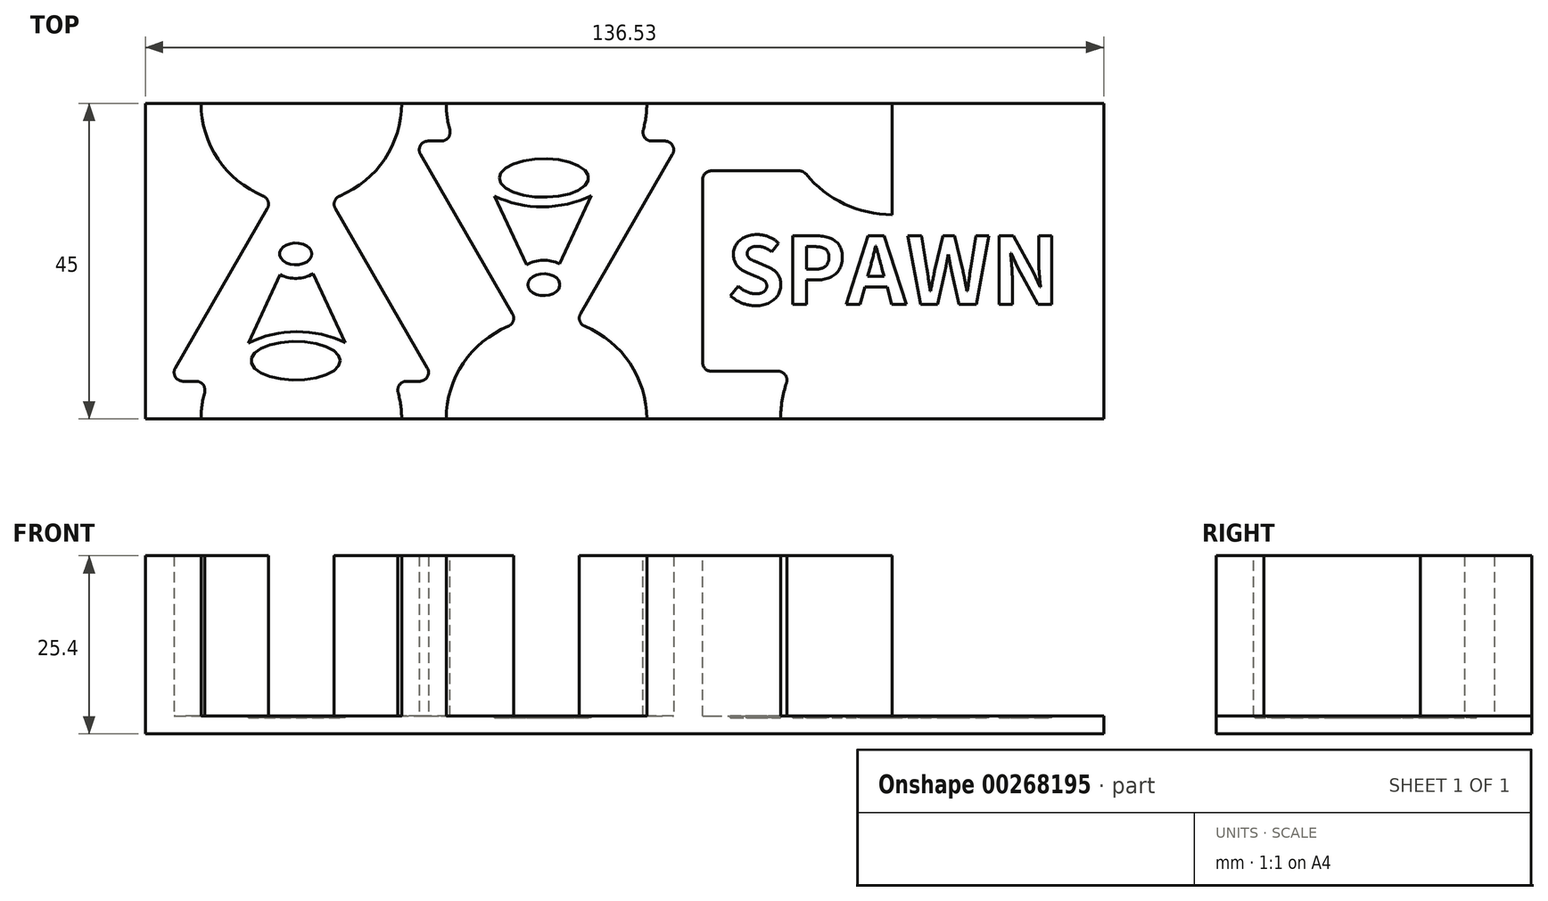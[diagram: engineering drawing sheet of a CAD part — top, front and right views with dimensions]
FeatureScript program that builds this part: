
annotation { "Feature Type Name" : "Feature", "Feature Type Description" : "" }
export const myFeature = defineFeature(function(context is Context, id is Id, definition is map)
    precondition{}
    {
        {
            var Q0;
            Q0=qCreatedBy(makeId("Top.planeOp"),FACE);
            var sketch = newSketch(context, id + "F0", { "sketchPlane" : qUnion([Q0])});
            skLineSegment(sketch, "E0.bottom", {"start": v(0, 0) * mm, "end": v(136.53, 0) * mm});
            skLineSegment(sketch, "E0.top", {"start": v(0, 45) * mm, "end": v(136.53, 45) * mm});
            skLineSegment(sketch, "E0.left", {"start": v(0, 0) * mm, "end": v(0, 45) * mm});
            skLineSegment(sketch, "E0.right", {"start": v(136.53, 0) * mm, "end": v(136.53, 45) * mm});
            skSolve(sketch);
        }
        {
            var Q0;
            Q0=makeQuery(id+"F0.imprint","IMPRINT",FACE,{"disambiguationData":[TD([[makeQuery(id+"F0.imprint","IMPRINT",EDGE,{"derivedFrom":sQuery(id+"F0.wireOp",EDGE,"E0.bottom")}),1.0]])]});
            extrude(context, id + "F1", {"entities" : qUnion([Q0]), "depth" : 25.4 * mm});
        }
        {
            var Q0;
            Q0=makeQuery(id+"F1.opExtrude","CAP_FACE",FACE,{"disambiguationData":[OSD([sQuery(id+"F0.wireOp",EDGE,"E0.bottom"),sQuery(id+"F0.wireOp",EDGE,"E0.top"),sQuery(id+"F0.wireOp",EDGE,"E0.left"),sQuery(id+"F0.wireOp",EDGE,"E0.right")])],"isStart":false});
            var sketch = newSketch(context, id + "F2", { "sketchPlane" : qUnion([Q0])});
            skCircle(sketch, "E1.cCircle", {"center": v(22.23, 16.38) * mm, "radius": 11 * mm, "construction": true});
            skLineSegment(sketch, "E1.0", {"start": v(22.23, 38.38) * mm, "end": v(41.28, 5.38) * mm});
            skLineSegment(sketch, "E1.1", {"start": v(41.28, 5.38) * mm, "end": v(3.17, 5.38) * mm});
            skLineSegment(sketch, "E1.2", {"start": v(3.17, 5.38) * mm, "end": v(22.23, 38.38) * mm});
            skPoint(sketch, "E1.0.midPoint", {"position": v(31.75, 21.88) * mm});
            skLineSegment(sketch, "E2", {"start": v(0, 22.5) * mm, "end": v(136.53, 22.5) * mm, "construction": true});
            skPoint(sketch, "E2.startSnap0", {"position": v(0, 22.5) * mm});
            skLineSegment(sketch, "E3", {"start": v(22.23, 45) * mm, "end": v(22.22, 0) * mm, "construction": true});
            skPoint(sketch, "E3.endSnap0", {"position": v(22.23, 5.38) * mm});
            skCircle(sketch, "E4", {"center": v(22.23, 45) * mm, "radius": 14.29 * mm});
            skCircle(sketch, "E5", {"center": v(22.22, 0) * mm, "radius": 14.29 * mm});
            skCircle(sketch, "E6.cCircle", {"center": v(57.15, 28.62) * mm, "radius": 11 * mm, "construction": true});
            skLineSegment(sketch, "E6.0", {"start": v(57.15, 6.63) * mm, "end": v(38.1, 39.62) * mm});
            skLineSegment(sketch, "E6.1", {"start": v(38.1, 39.62) * mm, "end": v(76.2, 39.62) * mm});
            skLineSegment(sketch, "E6.2", {"start": v(76.2, 39.62) * mm, "end": v(57.15, 6.63) * mm});
            skPoint(sketch, "E6.0.midPoint", {"position": v(47.63, 23.12) * mm});
            skLineSegment(sketch, "E7", {"start": v(136.53, 22.5) * mm, "end": v(0, 22.5) * mm, "construction": true});
            skPoint(sketch, "E7.startSnap0", {"position": v(122.49, -12.24) * mm});
            skLineSegment(sketch, "E8", {"start": v(57.15, 0) * mm, "end": v(57.15, 45) * mm, "construction": true});
            skPoint(sketch, "E8.endSnap0", {"position": v(57.15, 39.62) * mm});
            skCircle(sketch, "E9", {"center": v(57.15, 0) * mm, "radius": 14.29 * mm});
            skCircle(sketch, "E10", {"center": v(57.15, 45) * mm, "radius": 14.29 * mm});
            skLineSegment(sketch, "E11.bottom", {"start": v(79.38, 35.38) * mm, "end": v(133.35, 35.38) * mm});
            skLineSegment(sketch, "E11.top", {"start": v(79.38, 6.8) * mm, "end": v(133.35, 6.8) * mm});
            skLineSegment(sketch, "E11.left", {"start": v(79.38, 35.38) * mm, "end": v(79.38, 6.8) * mm});
            skLineSegment(sketch, "E11.right", {"start": v(133.35, 35.38) * mm, "end": v(133.35, 6.8) * mm});
            skCircle(sketch, "E12", {"center": v(106.36, 45) * mm, "radius": 15.88 * mm});
            skPoint(sketch, "E13.startSnap0", {"position": v(106.36, 6.8) * mm});
            skLineSegment(sketch, "E14", {"start": v(106.36, 0) * mm, "end": v(106.36, 45) * mm});
            skCircle(sketch, "E15", {"center": v(106.36, 0) * mm, "radius": 15.88 * mm});
            skSolve(sketch);
        }
        {
            var Q0;
            {var subQ1=sQuery(id+"F2.wireOp",EDGE,"E1.1");var subQ7=sQuery(id+"F2.wireOp",EDGE,"E1.0");var subQ8=makeQuery(id+"F2.imprint","INTERSECT",VERTEX,{"derivedFrom":[subQ7,subQ1]});Q0=makeQuery(id+"F2.imprint","IMPRINT",FACE,{"disambiguationData":[TD([[makeQuery(id+"F2.imprint","IMPRINT",EDGE,{"disambiguationData":[TD([[subQ8,1.0]])],"derivedFrom":subQ7}),-1.0]])]});}
            var Q1;
            {var subQ0=sQuery(id+"F2.wireOp",EDGE,"E5");var subQ1=sQuery(id+"F2.wireOp",EDGE,"E1.1");var subQ2=makeQuery(id+"F2.imprint","INTERSECT",VERTEX,{"disambiguationData":[OD(0.0)],"derivedFrom":[subQ1,subQ0]});Q1=makeQuery(id+"F2.imprint","IMPRINT",FACE,{"disambiguationData":[TD([[makeQuery(id+"F2.imprint","IMPRINT",EDGE,{"disambiguationData":[TD([[subQ2,-1.0]])],"derivedFrom":subQ1}),-1.0]])]});}
            var Q2;
            {var subQ0=sQuery(id+"F2.wireOp",EDGE,"E5");var subQ1=sQuery(id+"F2.wireOp",EDGE,"E1.1");var subQ2=makeQuery(id+"F2.imprint","INTERSECT",VERTEX,{"disambiguationData":[OD(0.0)],"derivedFrom":[subQ1,subQ0]});Q2=makeQuery(id+"F2.imprint","IMPRINT",FACE,{"disambiguationData":[TD([[makeQuery(id+"F2.imprint","IMPRINT",EDGE,{"disambiguationData":[TD([[subQ2,-1.0]])],"derivedFrom":subQ1}),1.0]])]});}
            var Q3;
            {var subQ1=sQuery(id+"F2.wireOp",EDGE,"E1.0");var subQ5=sQuery(id+"F2.wireOp",EDGE,"E1.2");var subQ8=makeQuery(id+"F2.imprint","INTERSECT",VERTEX,{"derivedFrom":[subQ1,subQ5]});Q3=makeQuery(id+"F2.imprint","IMPRINT",FACE,{"disambiguationData":[TD([[makeQuery(id+"F2.imprint","IMPRINT",EDGE,{"disambiguationData":[TD([[subQ8,-1.0]])],"derivedFrom":subQ1}),1.0]])]});}
            var Q4;
            {var subQ0=sQuery(id+"F2.wireOp",EDGE,"E1.2");var subQ1=sQuery(id+"F2.wireOp",EDGE,"E1.0");var subQ2=makeQuery(id+"F2.imprint","INTERSECT",VERTEX,{"derivedFrom":[subQ1,subQ0]});Q4=makeQuery(id+"F2.imprint","IMPRINT",FACE,{"disambiguationData":[TD([[makeQuery(id+"F2.imprint","IMPRINT",EDGE,{"disambiguationData":[TD([[subQ2,-1.0]])],"derivedFrom":subQ1}),-1.0]])]});}
            var Q5;
            {var subQ0=sQuery(id+"F2.wireOp",EDGE,"E10");var subQ1=sQuery(id+"F2.wireOp",EDGE,"E6.1");var subQ2=makeQuery(id+"F2.imprint","INTERSECT",VERTEX,{"disambiguationData":[OD(0.0)],"derivedFrom":[subQ1,subQ0]});Q5=makeQuery(id+"F2.imprint","IMPRINT",FACE,{"disambiguationData":[TD([[makeQuery(id+"F2.imprint","IMPRINT",EDGE,{"disambiguationData":[TD([[subQ2,-1.0]])],"derivedFrom":subQ1}),-1.0]])]});}
            var Q6;
            {var subQ0=sQuery(id+"F2.wireOp",EDGE,"E10");var subQ1=sQuery(id+"F2.wireOp",EDGE,"E6.1");var subQ2=makeQuery(id+"F2.imprint","INTERSECT",VERTEX,{"disambiguationData":[OD(0.0)],"derivedFrom":[subQ1,subQ0]});Q6=makeQuery(id+"F2.imprint","IMPRINT",FACE,{"disambiguationData":[TD([[makeQuery(id+"F2.imprint","IMPRINT",EDGE,{"disambiguationData":[TD([[subQ2,-1.0]])],"derivedFrom":subQ1}),1.0]])]});}
            var Q7;
            {var subQ1=sQuery(id+"F2.wireOp",EDGE,"E6.1");var subQ5=sQuery(id+"F2.wireOp",EDGE,"E6.0");var subQ6=makeQuery(id+"F2.imprint","INTERSECT",VERTEX,{"derivedFrom":[subQ5,subQ1]});Q7=makeQuery(id+"F2.imprint","IMPRINT",FACE,{"disambiguationData":[TD([[makeQuery(id+"F2.imprint","IMPRINT",EDGE,{"disambiguationData":[TD([[subQ6,1.0]])],"derivedFrom":subQ5}),-1.0]])]});}
            var Q8;
            {var subQ0=sQuery(id+"F2.wireOp",EDGE,"E6.2");var subQ1=sQuery(id+"F2.wireOp",EDGE,"E6.0");var subQ2=makeQuery(id+"F2.imprint","INTERSECT",VERTEX,{"derivedFrom":[subQ1,subQ0]});Q8=makeQuery(id+"F2.imprint","IMPRINT",FACE,{"disambiguationData":[TD([[makeQuery(id+"F2.imprint","IMPRINT",EDGE,{"disambiguationData":[TD([[subQ2,-1.0]])],"derivedFrom":subQ1}),-1.0]])]});}
            var Q9;
            {var subQ1=sQuery(id+"F2.wireOp",EDGE,"E6.2");var subQ6=sQuery(id+"F2.wireOp",EDGE,"E6.0");var subQ8=makeQuery(id+"F2.imprint","INTERSECT",VERTEX,{"derivedFrom":[subQ6,subQ1]});Q9=makeQuery(id+"F2.imprint","IMPRINT",FACE,{"disambiguationData":[TD([[makeQuery(id+"F2.imprint","IMPRINT",EDGE,{"disambiguationData":[TD([[subQ8,-1.0]])],"derivedFrom":subQ6}),1.0]])]});}
            var Q10;
            {var subQ5=sQuery(id+"F2.wireOp",EDGE,"E11.left");Q10=makeQuery(id+"F2.imprint","IMPRINT",FACE,{"disambiguationData":[TD([[makeQuery(id+"F2.imprint","IMPRINT",EDGE,{"derivedFrom":subQ5}),1.0]])]});}
            var Q11;
            {var subQ0=sQuery(id+"F2.wireOp",EDGE,"E12");var subQ1=sQuery(id+"F2.wireOp",EDGE,"E11.bottom");var subQ2=makeQuery(id+"F2.imprint","INTERSECT",VERTEX,{"disambiguationData":[OD(0.0)],"derivedFrom":[subQ1,subQ0]});Q11=makeQuery(id+"F2.imprint","IMPRINT",FACE,{"disambiguationData":[TD([[makeQuery(id+"F2.imprint","IMPRINT",EDGE,{"disambiguationData":[TD([[subQ2,-1.0]])],"derivedFrom":subQ1}),-1.0]])]});}
            var Q12;
            {var subQ0=sQuery(id+"F2.wireOp",EDGE,"E14");var subQ1=sQuery(id+"F2.wireOp",EDGE,"E11.bottom");var subQ2=makeQuery(id+"F2.imprint","INTERSECT",VERTEX,{"derivedFrom":[subQ1,subQ0]});Q12=makeQuery(id+"F2.imprint","IMPRINT",FACE,{"disambiguationData":[TD([[makeQuery(id+"F2.imprint","IMPRINT",EDGE,{"disambiguationData":[TD([[subQ2,-1.0]])],"derivedFrom":subQ1}),-1.0]])]});}
            var Q13;
            {var subQ0=sQuery(id+"F2.wireOp",EDGE,"E14");var subQ1=sQuery(id+"F2.wireOp",EDGE,"E11.bottom");var subQ2=makeQuery(id+"F2.imprint","INTERSECT",VERTEX,{"derivedFrom":[subQ1,subQ0]});Q13=makeQuery(id+"F2.imprint","IMPRINT",FACE,{"disambiguationData":[TD([[makeQuery(id+"F2.imprint","IMPRINT",EDGE,{"disambiguationData":[TD([[subQ2,-1.0]])],"derivedFrom":subQ1}),1.0]])]});}
            var Q14;
            {var subQ0=sQuery(id+"F2.wireOp",EDGE,"E12");var subQ1=sQuery(id+"F2.wireOp",EDGE,"E11.bottom");var subQ2=makeQuery(id+"F2.imprint","INTERSECT",VERTEX,{"disambiguationData":[OD(0.0)],"derivedFrom":[subQ1,subQ0]});Q14=makeQuery(id+"F2.imprint","IMPRINT",FACE,{"disambiguationData":[TD([[makeQuery(id+"F2.imprint","IMPRINT",EDGE,{"disambiguationData":[TD([[subQ2,-1.0]])],"derivedFrom":subQ1}),1.0]])]});}
            var Q15;
            {var subQ0=sQuery(id+"F2.wireOp",EDGE,"E11.right");Q15=makeQuery(id+"F2.imprint","IMPRINT",FACE,{"disambiguationData":[TD([[makeQuery(id+"F2.imprint","IMPRINT",EDGE,{"derivedFrom":subQ0}),-1.0]])]});}
            var Q16;
            {var subQ0=sQuery(id+"F2.wireOp",EDGE,"E14");var subQ1=sQuery(id+"F2.wireOp",EDGE,"E11.top");var subQ2=makeQuery(id+"F2.imprint","INTERSECT",VERTEX,{"derivedFrom":[subQ1,subQ0]});Q16=makeQuery(id+"F2.imprint","IMPRINT",FACE,{"disambiguationData":[TD([[makeQuery(id+"F2.imprint","IMPRINT",EDGE,{"disambiguationData":[TD([[subQ2,-1.0]])],"derivedFrom":subQ1}),1.0]])]});}
            var Q17;
            {var subQ0=sQuery(id+"F2.wireOp",EDGE,"E15");var subQ1=sQuery(id+"F2.wireOp",EDGE,"E11.top");var subQ2=makeQuery(id+"F2.imprint","INTERSECT",VERTEX,{"disambiguationData":[OD(0.0)],"derivedFrom":[subQ1,subQ0]});Q17=makeQuery(id+"F2.imprint","IMPRINT",FACE,{"disambiguationData":[TD([[makeQuery(id+"F2.imprint","IMPRINT",EDGE,{"disambiguationData":[TD([[subQ2,-1.0]])],"derivedFrom":subQ1}),1.0]])]});}
            var Q18;
            {var subQ0=sQuery(id+"F2.wireOp",EDGE,"E15");var subQ1=sQuery(id+"F2.wireOp",EDGE,"E11.top");var subQ2=makeQuery(id+"F2.imprint","INTERSECT",VERTEX,{"disambiguationData":[OD(0.0)],"derivedFrom":[subQ1,subQ0]});Q18=makeQuery(id+"F2.imprint","IMPRINT",FACE,{"disambiguationData":[TD([[makeQuery(id+"F2.imprint","IMPRINT",EDGE,{"disambiguationData":[TD([[subQ2,-1.0]])],"derivedFrom":subQ1}),-1.0]])]});}
            var Q19;
            {var subQ0=sQuery(id+"F2.wireOp",EDGE,"E14");var subQ1=sQuery(id+"F2.wireOp",EDGE,"E11.top");var subQ2=makeQuery(id+"F2.imprint","INTERSECT",VERTEX,{"derivedFrom":[subQ1,subQ0]});Q19=makeQuery(id+"F2.imprint","IMPRINT",FACE,{"disambiguationData":[TD([[makeQuery(id+"F2.imprint","IMPRINT",EDGE,{"disambiguationData":[TD([[subQ2,-1.0]])],"derivedFrom":subQ1}),-1.0]])]});}
            extrude(context, id + "F3", {"entities" : qUnion([Q0, Q1, Q2, Q3, Q4, Q5, Q6, Q7, Q8, Q9, Q10, Q11, Q12, Q13, Q14, Q15, Q16, Q17, Q18, Q19]), "operationType" : NewBodyOperationType.REMOVE, "oppositeDirection" : true, "depth" : 22.86 * mm});
        }
        {
            var Q0;
            Q0=makeQuery(id+"F3.boolean.opBoolean","COPY",FACE,{"derivedFrom":makeQuery(id+"F3.opExtrude","CAP_FACE",FACE,{"disambiguationData":[OSD([sQuery(id+"F0.wireOp",EDGE,"E0.bottom"),sQuery(id+"F0.wireOp",EDGE,"E0.top"),sQuery(id+"F2.wireOp",EDGE,"E11.bottom"),sQuery(id+"F2.wireOp",EDGE,"E11.top"),sQuery(id+"F2.wireOp",EDGE,"E11.left"),sQuery(id+"F2.wireOp",EDGE,"E11.right"),sQuery(id+"F2.wireOp",EDGE,"E12"),sQuery(id+"F2.wireOp",EDGE,"E15")])],"isStart":false})});
            var sketch = newSketch(context, id + "F4", { "sketchPlane" : qUnion([Q0])});
            skText(sketch, "E16", { "text": "SPAWN", "fontName": "NotoSansCJKsc-Bold.otf"});
            skLineSegment(sketch, "E17", {"start": v(106.36, 50.68) * mm, "end": v(106.36, -4.65) * mm, "construction": true});
            skPoint(sketch, "E17.startSnap0", {"position": v(106.36, 45) * mm});
            skPoint(sketch, "E17.endSnap0", {"position": v(106.36, 0) * mm});
            skLineSegment(sketch, "E18", {"start": v(79.38, 21.1) * mm, "end": v(133.35, 21.1) * mm, "construction": true});
            skPoint(sketch, "E18.startSnap0", {"position": v(82.8, 21.1) * mm});
            skPoint(sketch, "E18.endSnap0", {"position": v(129.92, 21.1) * mm});
            skLineSegment(sketch, "E19", {"start": v(14.67, 10.85) * mm, "end": v(19.2, 20.57) * mm});
            skLineSegment(sketch, "E20", {"start": v(23.9, 20.71) * mm, "end": v(28.48, 10.9) * mm});
            skArc(sketch, "E21", {"start": v(28.48, 10.9) * mm, "mid": v(21.57, 12.43) * mm, "end": v(14.67, 10.85) * mm});
            skEllipse(sketch, "E22", {"center": v(21.42, 23.54) * mm, "majorRadius": 2.29 * mm, "minorRadius": 1.56 * mm, "majorAxis": v(1, 0)});
            skArc(sketch, "E23", {"start": v(19.2, 20.57) * mm, "mid": v(21.57, 20.04) * mm, "end": v(23.9, 20.71) * mm});
            skEllipse(sketch, "E24", {"center": v(21.42, 8.32) * mm, "majorRadius": 6.36 * mm, "minorRadius": 2.75 * mm, "majorAxis": v(1, 0)});
            skLineSegment(sketch, "E25", {"start": v(63.52, 31.83) * mm, "end": v(59, 22.11) * mm});
            skLineSegment(sketch, "E26", {"start": v(54.3, 21.96) * mm, "end": v(49.71, 31.78) * mm});
            skArc(sketch, "E27", {"start": v(49.71, 31.78) * mm, "mid": v(56.62, 30.24) * mm, "end": v(63.52, 31.83) * mm});
            skEllipse(sketch, "E28", {"center": v(56.78, 19.14) * mm, "majorRadius": 2.29 * mm, "minorRadius": 1.56 * mm, "majorAxis": v(-1, 0)});
            skArc(sketch, "E29", {"start": v(59, 22.11) * mm, "mid": v(56.62, 22.63) * mm, "end": v(54.3, 21.96) * mm});
            skEllipse(sketch, "E30", {"center": v(56.78, 34.36) * mm, "majorRadius": 6.36 * mm, "minorRadius": 2.75 * mm, "majorAxis": v(-1, 0)});
            const initialGuessF4  = {"E16": [0.0828, 0.01633, 1, 0, 0.00952]};
            skSetInitialGuess(sketch, initialGuessF4);
            skSolve(sketch);
        }
        {
            var Q0;
            Q0=makeQuery(id+"F4.imprint","IMPRINT",FACE,{"disambiguationData":[TD([[makeQuery(id+"F4.imprint","IMPRINT",EDGE,{"derivedFrom":sQuery(id+"F4.wireOp",EDGE,"E16.sketch_text.stroke-0")}),1.0]])]});
            var Q1;
            Q1=makeQuery(id+"F4.imprint","IMPRINT",FACE,{"disambiguationData":[TD([[makeQuery(id+"F4.imprint","IMPRINT",EDGE,{"derivedFrom":sQuery(id+"F4.wireOp",EDGE,"E16.sketch_text.stroke-16")}),1.0]])]});
            var Q2;
            Q2=makeQuery(id+"F4.imprint","IMPRINT",FACE,{"disambiguationData":[TD([[makeQuery(id+"F4.imprint","IMPRINT",EDGE,{"derivedFrom":sQuery(id+"F4.wireOp",EDGE,"E16.sketch_text.stroke-28")}),1.0]])]});
            var Q3;
            Q3=makeQuery(id+"F4.imprint","IMPRINT",FACE,{"disambiguationData":[TD([[makeQuery(id+"F4.imprint","IMPRINT",EDGE,{"derivedFrom":sQuery(id+"F4.wireOp",EDGE,"E16.sketch_text.stroke-42")}),1.0]])]});
            var Q4;
            Q4=makeQuery(id+"F4.imprint","IMPRINT",FACE,{"disambiguationData":[TD([[makeQuery(id+"F4.imprint","IMPRINT",EDGE,{"derivedFrom":sQuery(id+"F4.wireOp",EDGE,"E16.sketch_text.stroke-64")}),1.0]])]});
            var Q5;
            Q5=makeQuery(id+"F4.imprint","IMPRINT",FACE,{"disambiguationData":[TD([[makeQuery(id+"F4.imprint","IMPRINT",EDGE,{"derivedFrom":sQuery(id+"F4.wireOp",EDGE,"E30")}),1.0]])]});
            var Q6;
            Q6=makeQuery(id+"F4.imprint","IMPRINT",FACE,{"disambiguationData":[TD([[makeQuery(id+"F4.imprint","IMPRINT",EDGE,{"derivedFrom":sQuery(id+"F4.wireOp",EDGE,"E25")}),-1.0]])]});
            var Q7;
            Q7=makeQuery(id+"F4.imprint","IMPRINT",FACE,{"disambiguationData":[TD([[makeQuery(id+"F4.imprint","IMPRINT",EDGE,{"derivedFrom":sQuery(id+"F4.wireOp",EDGE,"E28")}),1.0]])]});
            var Q8;
            Q8=makeQuery(id+"F4.imprint","IMPRINT",FACE,{"disambiguationData":[TD([[makeQuery(id+"F4.imprint","IMPRINT",EDGE,{"derivedFrom":sQuery(id+"F4.wireOp",EDGE,"E24")}),1.0]])]});
            var Q9;
            Q9=makeQuery(id+"F4.imprint","IMPRINT",FACE,{"disambiguationData":[TD([[makeQuery(id+"F4.imprint","IMPRINT",EDGE,{"derivedFrom":sQuery(id+"F4.wireOp",EDGE,"E19")}),-1.0]])]});
            var Q10;
            Q10=makeQuery(id+"F4.imprint","IMPRINT",FACE,{"disambiguationData":[TD([[makeQuery(id+"F4.imprint","IMPRINT",EDGE,{"derivedFrom":sQuery(id+"F4.wireOp",EDGE,"E22")}),1.0]])]});
            extrude(context, id + "F5", {"entities" : qUnion([Q0, Q1, Q2, Q3, Q4, Q5, Q6, Q7, Q8, Q9, Q10]), "operationType" : NewBodyOperationType.REMOVE, "oppositeDirection" : true, "depth" : 0.25 * mm});
        }
        {
            var Q0;
            {var subQ0=sQuery(id+"F2.wireOp",EDGE,"E5");var subQ1=sQuery(id+"F2.wireOp",EDGE,"E1.1");Q0=makeQuery(id+"F3.boolean.opBoolean","COPY",EDGE,{"derivedFrom":makeQuery(id+"F3.opExtrude","SWEPT_EDGE",EDGE,{"disambiguationData":[OSD([subQ1,subQ0]),TDD([makeQuery(id+"F2.imprint","INTERSECT",VERTEX,{"disambiguationData":[OD(1.0)],"derivedFrom":[subQ1,subQ0]})])]})});}
            var Q1;
            {var subQ0=sQuery(id+"F2.wireOp",EDGE,"E5");var subQ1=sQuery(id+"F2.wireOp",EDGE,"E1.1");Q1=makeQuery(id+"F3.boolean.opBoolean","COPY",EDGE,{"derivedFrom":makeQuery(id+"F3.opExtrude","SWEPT_EDGE",EDGE,{"disambiguationData":[OSD([subQ1,subQ0]),TDD([makeQuery(id+"F2.imprint","INTERSECT",VERTEX,{"disambiguationData":[OD(0.0)],"derivedFrom":[subQ1,subQ0]})])]})});}
            var Q2;
            Q2=makeQuery(id+"F3.boolean.opBoolean","COPY",EDGE,{"derivedFrom":makeQuery(id+"F3.opExtrude","SWEPT_EDGE",EDGE,{"disambiguationData":[OSD([sQuery(id+"F2.wireOp",EDGE,"E1.2"),sQuery(id+"F2.wireOp",EDGE,"E4")])]})});
            var Q3;
            Q3=makeQuery(id+"F3.boolean.opBoolean","COPY",EDGE,{"derivedFrom":makeQuery(id+"F3.opExtrude","SWEPT_EDGE",EDGE,{"disambiguationData":[OSD([sQuery(id+"F2.wireOp",EDGE,"E1.0"),sQuery(id+"F2.wireOp",EDGE,"E4")])]})});
            var Q4;
            {var subQ0=sQuery(id+"F2.wireOp",EDGE,"E4");var subQ1=sQuery(id+"F0.wireOp",EDGE,"E0.top");Q4=makeQuery(id+"F3.boolean.opBoolean","COPY",EDGE,{"derivedFrom":makeQuery(id+"F3.opExtrude","SWEPT_EDGE",EDGE,{"disambiguationData":[OSD([subQ1,subQ0]),TDD([makeQuery(id+"F2.imprint","INTERSECT",VERTEX,{"disambiguationData":[OD(0.0)],"derivedFrom":[makeQuery(id+"F1.opExtrude","CAP_EDGE",EDGE,{"disambiguationData":[OSD([subQ1])],"isStart":false}),subQ0]})])]})});}
            var Q5;
            {var subQ0=sQuery(id+"F2.wireOp",EDGE,"E4");var subQ1=sQuery(id+"F0.wireOp",EDGE,"E0.top");Q5=makeQuery(id+"F3.boolean.opBoolean","COPY",EDGE,{"derivedFrom":makeQuery(id+"F3.opExtrude","SWEPT_EDGE",EDGE,{"disambiguationData":[OSD([subQ1,subQ0]),TDD([makeQuery(id+"F2.imprint","INTERSECT",VERTEX,{"disambiguationData":[OD(1.0)],"derivedFrom":[makeQuery(id+"F1.opExtrude","CAP_EDGE",EDGE,{"disambiguationData":[OSD([subQ1])],"isStart":false}),subQ0]})])]})});}
            var Q6;
            {var subQ0=sQuery(id+"F2.wireOp",EDGE,"E10");var subQ1=sQuery(id+"F0.wireOp",EDGE,"E0.top");Q6=makeQuery(id+"F3.boolean.opBoolean","COPY",EDGE,{"derivedFrom":makeQuery(id+"F3.opExtrude","SWEPT_EDGE",EDGE,{"disambiguationData":[OSD([subQ1,subQ0]),TDD([makeQuery(id+"F2.imprint","INTERSECT",VERTEX,{"disambiguationData":[OD(0.0)],"derivedFrom":[makeQuery(id+"F1.opExtrude","CAP_EDGE",EDGE,{"disambiguationData":[OSD([subQ1])],"isStart":false}),subQ0]})])]})});}
            var Q7;
            {var subQ0=sQuery(id+"F2.wireOp",EDGE,"E10");var subQ1=sQuery(id+"F2.wireOp",EDGE,"E6.1");Q7=makeQuery(id+"F3.boolean.opBoolean","COPY",EDGE,{"derivedFrom":makeQuery(id+"F3.opExtrude","SWEPT_EDGE",EDGE,{"disambiguationData":[OSD([subQ1,subQ0]),TDD([makeQuery(id+"F2.imprint","INTERSECT",VERTEX,{"disambiguationData":[OD(0.0)],"derivedFrom":[subQ1,subQ0]})])]})});}
            var Q8;
            Q8=makeQuery(id+"F3.boolean.opBoolean","COPY",EDGE,{"derivedFrom":makeQuery(id+"F3.opExtrude","SWEPT_EDGE",EDGE,{"disambiguationData":[OSD([sQuery(id+"F2.wireOp",EDGE,"E6.0"),sQuery(id+"F2.wireOp",EDGE,"E6.1")])]})});
            var Q9;
            Q9=makeQuery(id+"F3.boolean.opBoolean","COPY",EDGE,{"derivedFrom":makeQuery(id+"F3.opExtrude","SWEPT_EDGE",EDGE,{"disambiguationData":[OSD([sQuery(id+"F2.wireOp",EDGE,"E6.0"),sQuery(id+"F2.wireOp",EDGE,"E9")])]})});
            var Q10;
            Q10=makeQuery(id+"F3.boolean.opBoolean","COPY",EDGE,{"derivedFrom":makeQuery(id+"F3.opExtrude","SWEPT_EDGE",EDGE,{"disambiguationData":[OSD([sQuery(id+"F2.wireOp",EDGE,"E1.0"),sQuery(id+"F2.wireOp",EDGE,"E1.1")])]})});
            var Q11;
            Q11=makeQuery(id+"F3.boolean.opBoolean","COPY",EDGE,{"derivedFrom":makeQuery(id+"F3.opExtrude","SWEPT_EDGE",EDGE,{"disambiguationData":[OSD([sQuery(id+"F2.wireOp",EDGE,"E6.1"),sQuery(id+"F2.wireOp",EDGE,"E6.2")])]})});
            var Q12;
            {var subQ0=sQuery(id+"F2.wireOp",EDGE,"E10");var subQ1=sQuery(id+"F2.wireOp",EDGE,"E6.1");Q12=makeQuery(id+"F3.boolean.opBoolean","COPY",EDGE,{"derivedFrom":makeQuery(id+"F3.opExtrude","SWEPT_EDGE",EDGE,{"disambiguationData":[OSD([subQ1,subQ0]),TDD([makeQuery(id+"F2.imprint","INTERSECT",VERTEX,{"disambiguationData":[OD(1.0)],"derivedFrom":[subQ1,subQ0]})])]})});}
            var Q13;
            {var subQ0=sQuery(id+"F2.wireOp",EDGE,"E10");var subQ1=sQuery(id+"F0.wireOp",EDGE,"E0.top");Q13=makeQuery(id+"F3.boolean.opBoolean","COPY",EDGE,{"derivedFrom":makeQuery(id+"F3.opExtrude","SWEPT_EDGE",EDGE,{"disambiguationData":[OSD([subQ1,subQ0]),TDD([makeQuery(id+"F2.imprint","INTERSECT",VERTEX,{"disambiguationData":[OD(1.0)],"derivedFrom":[makeQuery(id+"F1.opExtrude","CAP_EDGE",EDGE,{"disambiguationData":[OSD([subQ1])],"isStart":false}),subQ0]})])]})});}
            var Q14;
            Q14=makeQuery(id+"F3.boolean.opBoolean","COPY",EDGE,{"derivedFrom":makeQuery(id+"F3.opExtrude","SWEPT_EDGE",EDGE,{"disambiguationData":[OSD([sQuery(id+"F2.wireOp",EDGE,"E6.2"),sQuery(id+"F2.wireOp",EDGE,"E9")])]})});
            var Q15;
            {var subQ0=sQuery(id+"F2.wireOp",EDGE,"E9");var subQ1=sQuery(id+"F0.wireOp",EDGE,"E0.bottom");Q15=makeQuery(id+"F3.boolean.opBoolean","COPY",EDGE,{"derivedFrom":makeQuery(id+"F3.opExtrude","SWEPT_EDGE",EDGE,{"disambiguationData":[OSD([subQ1,subQ0]),TDD([makeQuery(id+"F2.imprint","INTERSECT",VERTEX,{"disambiguationData":[OD(0.0)],"derivedFrom":[makeQuery(id+"F1.opExtrude","CAP_EDGE",EDGE,{"disambiguationData":[OSD([subQ1])],"isStart":false}),subQ0]})])]})});}
            var Q16;
            {var subQ0=sQuery(id+"F2.wireOp",EDGE,"E5");var subQ1=sQuery(id+"F0.wireOp",EDGE,"E0.bottom");Q16=makeQuery(id+"F3.boolean.opBoolean","COPY",EDGE,{"derivedFrom":makeQuery(id+"F3.opExtrude","SWEPT_EDGE",EDGE,{"disambiguationData":[OSD([subQ1,subQ0]),TDD([makeQuery(id+"F2.imprint","INTERSECT",VERTEX,{"disambiguationData":[OD(1.0)],"derivedFrom":[makeQuery(id+"F1.opExtrude","CAP_EDGE",EDGE,{"disambiguationData":[OSD([subQ1])],"isStart":false}),subQ0]})])]})});}
            var Q17;
            {var subQ0=sQuery(id+"F2.wireOp",EDGE,"E5");var subQ1=sQuery(id+"F0.wireOp",EDGE,"E0.bottom");Q17=makeQuery(id+"F3.boolean.opBoolean","COPY",EDGE,{"derivedFrom":makeQuery(id+"F3.opExtrude","SWEPT_EDGE",EDGE,{"disambiguationData":[OSD([subQ1,subQ0]),TDD([makeQuery(id+"F2.imprint","INTERSECT",VERTEX,{"disambiguationData":[OD(0.0)],"derivedFrom":[makeQuery(id+"F1.opExtrude","CAP_EDGE",EDGE,{"disambiguationData":[OSD([subQ1])],"isStart":false}),subQ0]})])]})});}
            var Q18;
            {var subQ0=sQuery(id+"F2.wireOp",EDGE,"E9");var subQ1=sQuery(id+"F0.wireOp",EDGE,"E0.bottom");Q18=makeQuery(id+"F3.boolean.opBoolean","COPY",EDGE,{"derivedFrom":makeQuery(id+"F3.opExtrude","SWEPT_EDGE",EDGE,{"disambiguationData":[OSD([subQ1,subQ0]),TDD([makeQuery(id+"F2.imprint","INTERSECT",VERTEX,{"disambiguationData":[OD(1.0)],"derivedFrom":[makeQuery(id+"F1.opExtrude","CAP_EDGE",EDGE,{"disambiguationData":[OSD([subQ1])],"isStart":false}),subQ0]})])]})});}
            var Q19;
            Q19=makeQuery(id+"F3.boolean.opBoolean","COPY",EDGE,{"derivedFrom":makeQuery(id+"F3.opExtrude","SWEPT_EDGE",EDGE,{"disambiguationData":[OSD([sQuery(id+"F2.wireOp",EDGE,"E11.bottom"),sQuery(id+"F2.wireOp",EDGE,"E11.left")])]})});
            var Q20;
            {var subQ0=sQuery(id+"F2.wireOp",EDGE,"E12");var subQ1=sQuery(id+"F2.wireOp",EDGE,"E11.bottom");Q20=makeQuery(id+"F3.boolean.opBoolean","COPY",EDGE,{"derivedFrom":makeQuery(id+"F3.opExtrude","SWEPT_EDGE",EDGE,{"disambiguationData":[OSD([subQ1,subQ0]),TDD([makeQuery(id+"F2.imprint","INTERSECT",VERTEX,{"disambiguationData":[OD(0.0)],"derivedFrom":[subQ1,subQ0]})])]})});}
            var Q21;
            {var subQ0=sQuery(id+"F2.wireOp",EDGE,"E12");var subQ1=sQuery(id+"F0.wireOp",EDGE,"E0.top");Q21=makeQuery(id+"F3.boolean.opBoolean","COPY",EDGE,{"derivedFrom":makeQuery(id+"F3.opExtrude","SWEPT_EDGE",EDGE,{"disambiguationData":[OSD([subQ1,subQ0]),TDD([makeQuery(id+"F2.imprint","INTERSECT",VERTEX,{"disambiguationData":[OD(0.0)],"derivedFrom":[makeQuery(id+"F1.opExtrude","CAP_EDGE",EDGE,{"disambiguationData":[OSD([subQ1])],"isStart":false}),subQ0]})])]})});}
            var Q22;
            Q22=makeQuery(id+"F3.boolean.opBoolean","COPY",EDGE,{"derivedFrom":makeQuery(id+"F3.opExtrude","SWEPT_EDGE",EDGE,{"disambiguationData":[OSD([sQuery(id+"F2.wireOp",EDGE,"E11.top"),sQuery(id+"F2.wireOp",EDGE,"E11.left")])]})});
            var Q23;
            {var subQ0=sQuery(id+"F2.wireOp",EDGE,"E15");var subQ1=sQuery(id+"F2.wireOp",EDGE,"E11.top");Q23=makeQuery(id+"F3.boolean.opBoolean","COPY",EDGE,{"derivedFrom":makeQuery(id+"F3.opExtrude","SWEPT_EDGE",EDGE,{"disambiguationData":[OSD([subQ1,subQ0]),TDD([makeQuery(id+"F2.imprint","INTERSECT",VERTEX,{"disambiguationData":[OD(0.0)],"derivedFrom":[subQ1,subQ0]})])]})});}
            var Q24;
            {var subQ0=sQuery(id+"F2.wireOp",EDGE,"E12");var subQ1=sQuery(id+"F2.wireOp",EDGE,"E11.bottom");Q24=makeQuery(id+"F3.boolean.opBoolean","COPY",EDGE,{"derivedFrom":makeQuery(id+"F3.opExtrude","SWEPT_EDGE",EDGE,{"disambiguationData":[OSD([subQ1,subQ0]),TDD([makeQuery(id+"F2.imprint","INTERSECT",VERTEX,{"disambiguationData":[OD(1.0)],"derivedFrom":[subQ1,subQ0]})])]})});}
            var Q25;
            {var subQ0=sQuery(id+"F2.wireOp",EDGE,"E12");var subQ1=sQuery(id+"F0.wireOp",EDGE,"E0.top");Q25=makeQuery(id+"F3.boolean.opBoolean","COPY",EDGE,{"derivedFrom":makeQuery(id+"F3.opExtrude","SWEPT_EDGE",EDGE,{"disambiguationData":[OSD([subQ1,subQ0]),TDD([makeQuery(id+"F2.imprint","INTERSECT",VERTEX,{"disambiguationData":[OD(1.0)],"derivedFrom":[makeQuery(id+"F1.opExtrude","CAP_EDGE",EDGE,{"disambiguationData":[OSD([subQ1])],"isStart":false}),subQ0]})])]})});}
            var Q26;
            Q26=makeQuery(id+"F3.boolean.opBoolean","COPY",EDGE,{"derivedFrom":makeQuery(id+"F3.opExtrude","SWEPT_EDGE",EDGE,{"disambiguationData":[OSD([sQuery(id+"F2.wireOp",EDGE,"E11.bottom"),sQuery(id+"F2.wireOp",EDGE,"E11.right")])]})});
            var Q27;
            Q27=makeQuery(id+"F3.boolean.opBoolean","COPY",EDGE,{"derivedFrom":makeQuery(id+"F3.opExtrude","SWEPT_EDGE",EDGE,{"disambiguationData":[OSD([sQuery(id+"F2.wireOp",EDGE,"E11.top"),sQuery(id+"F2.wireOp",EDGE,"E11.right")])]})});
            var Q28;
            {var subQ0=sQuery(id+"F2.wireOp",EDGE,"E15");var subQ1=sQuery(id+"F2.wireOp",EDGE,"E11.top");Q28=makeQuery(id+"F3.boolean.opBoolean","COPY",EDGE,{"derivedFrom":makeQuery(id+"F3.opExtrude","SWEPT_EDGE",EDGE,{"disambiguationData":[OSD([subQ1,subQ0]),TDD([makeQuery(id+"F2.imprint","INTERSECT",VERTEX,{"disambiguationData":[OD(1.0)],"derivedFrom":[subQ1,subQ0]})])]})});}
            var Q29;
            {var subQ0=sQuery(id+"F2.wireOp",EDGE,"E15");var subQ1=sQuery(id+"F0.wireOp",EDGE,"E0.bottom");Q29=makeQuery(id+"F3.boolean.opBoolean","COPY",EDGE,{"derivedFrom":makeQuery(id+"F3.opExtrude","SWEPT_EDGE",EDGE,{"disambiguationData":[OSD([subQ1,subQ0]),TDD([makeQuery(id+"F2.imprint","INTERSECT",VERTEX,{"disambiguationData":[OD(0.0)],"derivedFrom":[makeQuery(id+"F1.opExtrude","CAP_EDGE",EDGE,{"disambiguationData":[OSD([subQ1])],"isStart":false}),subQ0]})])]})});}
            var Q30;
            Q30=makeQuery(id+"F3.boolean.opBoolean","COPY",EDGE,{"derivedFrom":makeQuery(id+"F3.opExtrude","SWEPT_EDGE",EDGE,{"disambiguationData":[OSD([sQuery(id+"F2.wireOp",EDGE,"E1.1"),sQuery(id+"F2.wireOp",EDGE,"E1.2")])]})});
            fillet(context, id + "F6", {"entities" : qUnion([Q0, Q1, Q2, Q3, Q4, Q5, Q6, Q7, Q8, Q9, Q10, Q11, Q12, Q13, Q14, Q15, Q16, Q17, Q18, Q19, Q20, Q21, Q22, Q23, Q24, Q25, Q26, Q27, Q28, Q29, Q30]), "radius" : 1.27 * mm, "tangentPropagation" : true, "allowEdgeOverflow" : false});
        }
    });
